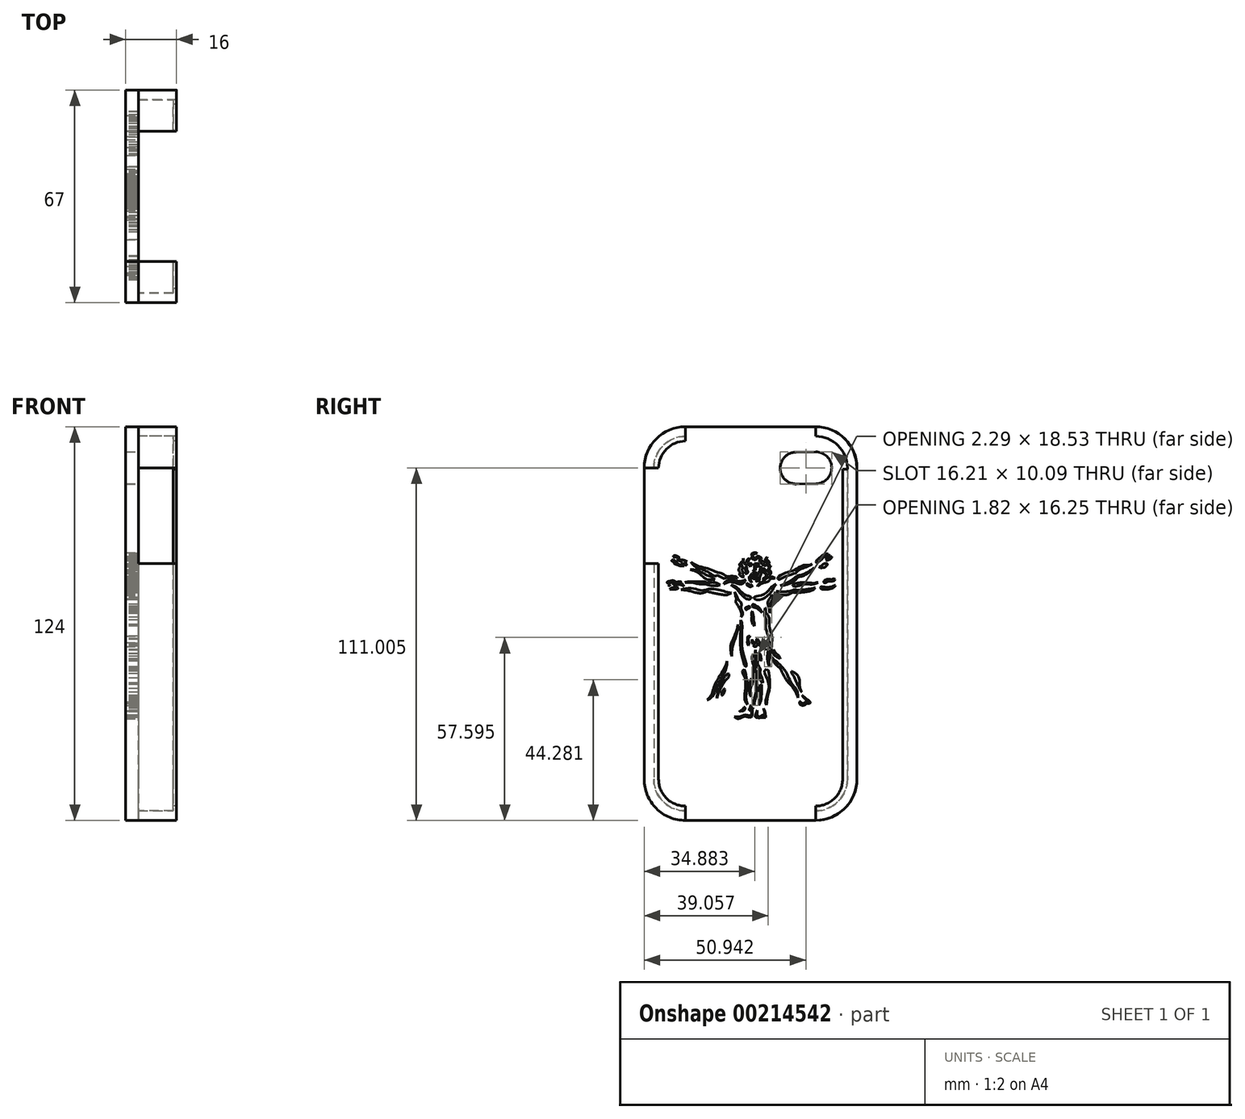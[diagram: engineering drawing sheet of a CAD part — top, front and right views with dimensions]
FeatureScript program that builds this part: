
annotation { "Feature Type Name" : "Feature", "Feature Type Description" : "" }
export const myFeature = defineFeature(function(context is Context, id is Id, definition is map)
    precondition{}
    {
        {
            var Q0;
            Q0=qCreatedBy(makeId("Right.planeOp"),FACE);
            var sketch = newSketch(context, id + "F0", { "sketchPlane" : qUnion([Q0])});
            skLineSegment(sketch, "E0.rect.bottom", {"start": v(20.5, 62) * mm, "end": v(-20.5, 62) * mm});
            skLineSegment(sketch, "E0.rect.top", {"start": v(20.5, -62) * mm, "end": v(-20.5, -62) * mm});
            skLineSegment(sketch, "E0.rect.left", {"start": v(33.5, 49) * mm, "end": v(33.5, -49) * mm});
            skLineSegment(sketch, "E0.rect.right", {"start": v(-33.5, 49) * mm, "end": v(-33.5, -49) * mm});
            skPoint(sketch, "E0.rect.middle", {"position": v(0, 0) * mm});
            skPoint(sketch, "E1.visualSharp", {"position": v(-33.5, 62) * mm});
            skArc(sketch, "E1.filletArc", {"start": v(-20.5, 62) * mm, "mid": v(-29.7, 58.2) * mm, "end": v(-33.5, 49) * mm});
            skPoint(sketch, "E2.visualSharp", {"position": v(-33.5, -62) * mm});
            skArc(sketch, "E2.filletArc", {"start": v(-33.5, -49) * mm, "mid": v(-29.7, -58.2) * mm, "end": v(-20.5, -62) * mm});
            skPoint(sketch, "E3.visualSharp", {"position": v(33.5, 62) * mm});
            skArc(sketch, "E3.filletArc", {"start": v(33.5, 49) * mm, "mid": v(29.7, 58.2) * mm, "end": v(20.5, 62) * mm});
            skPoint(sketch, "E4.visualSharp", {"position": v(33.5, -62) * mm});
            skArc(sketch, "E4.filletArc", {"start": v(20.5, -62) * mm, "mid": v(29.7, -58.2) * mm, "end": v(33.5, -49) * mm});
            skSolve(sketch);
        }
        {
            var Q0;
            Q0=qSketchRegion(id+"F0",true);
            extrude(context, id + "F1", {"entities" : qUnion([Q0]), "depth" : 4 * mm});
        }
        {
            var Q0;
            Q0=qCreatedBy(makeId("Right.planeOp"),FACE);
            var sketch = newSketch(context, id + "F2", { "sketchPlane" : qUnion([Q0])});
            skArc(sketch, "E5", {"start": v(20.7, 44.05) * mm, "mid": v(25.55, 49.12) * mm, "end": v(20.55, 54.05) * mm});
            skLineSegment(sketch, "E6", {"start": v(20.55, 54.05) * mm, "end": v(14.26, 53.96) * mm});
            skLineSegment(sketch, "E7", {"start": v(20.7, 44.05) * mm, "end": v(14.4, 43.96) * mm});
            skArc(sketch, "E8", {"start": v(14.26, 53.96) * mm, "mid": v(9.34, 48.89) * mm, "end": v(14.4, 43.96) * mm});
            skLineSegment(sketch, "E9", {"start": v(14.26, 53.96) * mm, "end": v(14.4, 43.96) * mm, "construction": true});
            skLineSegment(sketch, "E10", {"start": v(20.55, 54.05) * mm, "end": v(20.7, 44.05) * mm, "construction": true});
            skSolve(sketch);
        }
        {
            var Q0;
            Q0=makeQuery(id+"F2.imprint","IMPRINT",FACE,{"disambiguationData":[TD([[makeQuery(id+"F2.imprint","IMPRINT",EDGE,{"derivedFrom":sQuery(id+"F2.wireOp",EDGE,"E5")}),1.0]])]});
            extrude(context, id + "F3", {"entities" : qUnion([Q0]), "operationType" : NewBodyOperationType.REMOVE, "oppositeDirection" : true, "depth" : 25.4 * mm, "hasSecondDirection" : true, "secondDirectionOppositeDirection" : false, "secondDirectionDepth" : 33.72 * mm});
        }
        {
            var Q0;
            Q0=qCreatedBy(makeId("Right.planeOp"),FACE);
            var sketch = newSketch(context, id + "F4", { "sketchPlane" : qUnion([Q0])});
            skLineSegment(sketch, "E11", {"start": v(-30.46, 18.92) * mm, "end": v(-33.5, 18.92) * mm});
            skLineSegment(sketch, "E12", {"start": v(-33.5, 18.92) * mm, "end": v(-33.5, -49) * mm});
            skLineSegment(sketch, "E13", {"start": v(-33.5, -49) * mm, "end": v(-30.46, -49) * mm});
            skLineSegment(sketch, "E14", {"start": v(-30.46, -49) * mm, "end": v(-30.46, 18.92) * mm});
            skSolve(sketch);
        }
        {
            var Q0;
            Q0=qSketchRegion(id+"F4",true);
            extrude(context, id + "F5", {"entities" : qUnion([Q0]), "operationType" : NewBodyOperationType.ADD, "depth" : 16 * mm});
        }
        {
            var Q0;
            Q0=qCreatedBy(makeId("Right.planeOp"),FACE);
            var sketch = newSketch(context, id + "F6", { "sketchPlane" : qUnion([Q0])});
            skLineSegment(sketch, "E15", {"start": v(-33.5, -49) * mm, "end": v(-30.46, -49) * mm});
            skLineSegment(sketch, "E16", {"start": v(-20.5, -59) * mm, "end": v(-20.5, -62) * mm});
            skArc(sketch, "E17", {"start": v(-30.46, -49) * mm, "mid": v(-27.56, -56.07) * mm, "end": v(-20.5, -59) * mm});
            skArc(sketch, "E18", {"start": v(-33.5, -49) * mm, "mid": v(-29.7, -58.2) * mm, "end": v(-20.5, -62) * mm});
            skSolve(sketch);
        }
        {
            var Q0;
            Q0=qSketchRegion(id+"F6",true);
            extrude(context, id + "F7", {"entities" : qUnion([Q0]), "operationType" : NewBodyOperationType.ADD, "depth" : 16 * mm});
        }
        {
            var Q0;
            Q0=qCreatedBy(makeId("Right.planeOp"),FACE);
            var sketch = newSketch(context, id + "F8", { "sketchPlane" : qUnion([Q0])});
            skLineSegment(sketch, "E19", {"start": v(-30.47, 48.93) * mm, "end": v(-33.5, 48.93) * mm});
            skLineSegment(sketch, "E20", {"start": v(-20.5, 62) * mm, "end": v(-20.5, 58.97) * mm});
            skArc(sketch, "E21", {"start": v(-20.5, 58.97) * mm, "mid": v(-27.55, 56) * mm, "end": v(-30.47, 48.93) * mm});
            skArc(sketch, "E22", {"start": v(-20.5, 62) * mm, "mid": v(-29.7, 58.15) * mm, "end": v(-33.5, 48.93) * mm});
            skSolve(sketch);
        }
        {
            var Q0;
            Q0=qSketchRegion(id+"F8",true);
            extrude(context, id + "F9", {"entities" : qUnion([Q0]), "operationType" : NewBodyOperationType.ADD, "depth" : 16 * mm});
        }
        {
            var Q0;
            Q0=qCreatedBy(makeId("Right.planeOp"),FACE);
            var sketch = newSketch(context, id + "F10", { "sketchPlane" : qUnion([Q0])});
            skLineSegment(sketch, "E23", {"start": v(20.49, -62) * mm, "end": v(20.49, -59) * mm});
            skLineSegment(sketch, "E24", {"start": v(33.5, -49) * mm, "end": v(30.5, -49) * mm});
            skArc(sketch, "E25", {"start": v(20.49, -59) * mm, "mid": v(27.55, -56.06) * mm, "end": v(30.5, -49) * mm});
            skArc(sketch, "E26", {"start": v(20.49, -62) * mm, "mid": v(29.67, -58.19) * mm, "end": v(33.5, -49) * mm});
            skSolve(sketch);
        }
        {
            var Q0;
            Q0=qSketchRegion(id+"F10",true);
            extrude(context, id + "F11", {"entities" : qUnion([Q0]), "operationType" : NewBodyOperationType.ADD, "depth" : 16 * mm});
        }
        {
            var Q0;
            Q0=qCreatedBy(makeId("Right.planeOp"),FACE);
            var sketch = newSketch(context, id + "F12", { "sketchPlane" : qUnion([Q0])});
            skLineSegment(sketch, "E27", {"start": v(33.46, 49) * mm, "end": v(30.5, 49) * mm});
            skLineSegment(sketch, "E28", {"start": v(20.5, 62) * mm, "end": v(20.5, 58.99) * mm});
            skArc(sketch, "E29", {"start": v(33.46, 49) * mm, "mid": v(29.66, 58.17) * mm, "end": v(20.5, 62) * mm});
            skArc(sketch, "E30", {"start": v(30.5, 49) * mm, "mid": v(27.55, 56.05) * mm, "end": v(20.5, 58.99) * mm});
            skSolve(sketch);
        }
        {
            var Q0;
            Q0=qSketchRegion(id+"F12",true);
            extrude(context, id + "F13", {"entities" : qUnion([Q0]), "operationType" : NewBodyOperationType.ADD, "depth" : 16 * mm});
        }
        {
            var Q0;
            Q0=qCreatedBy(makeId("Right.planeOp"),FACE);
            var sketch = newSketch(context, id + "F14", { "sketchPlane" : qUnion([Q0])});
            skLineSegment(sketch, "E31", {"start": v(30.5, -49) * mm, "end": v(33.49, -49) * mm});
            skLineSegment(sketch, "E32", {"start": v(33.49, -49) * mm, "end": v(33.49, 49) * mm});
            skLineSegment(sketch, "E33", {"start": v(33.49, 49) * mm, "end": v(30.5, 49) * mm});
            skLineSegment(sketch, "E34", {"start": v(30.5, 49) * mm, "end": v(30.5, -49) * mm});
            skSolve(sketch);
        }
        {
            var Q0;
            Q0=qSketchRegion(id+"F14",true);
            extrude(context, id + "F15", {"entities" : qUnion([Q0]), "operationType" : NewBodyOperationType.ADD, "depth" : 16 * mm});
        }
        {
            var Q0;
            Q0=qCreatedBy(makeId("Right.planeOp"),FACE);
            var sketch = newSketch(context, id + "F16", { "sketchPlane" : qUnion([Q0])});
            skLineSegment(sketch, "E35", {"start": v(-30.46, 18.92) * mm, "end": v(-30.46, -49.07) * mm});
            skLineSegment(sketch, "E36", {"start": v(-30.46, -49.07) * mm, "end": v(-28.96, -49.07) * mm});
            skLineSegment(sketch, "E37", {"start": v(-28.96, -49.07) * mm, "end": v(-28.96, 18.92) * mm});
            skLineSegment(sketch, "E38", {"start": v(-28.96, 18.92) * mm, "end": v(-30.46, 18.92) * mm});
            skLineSegment(sketch, "E39", {"start": v(-20.5, -59) * mm, "end": v(-20.5, -57.5) * mm});
            skArc(sketch, "E40", {"start": v(-30.46, -49.07) * mm, "mid": v(-27.53, -56.1) * mm, "end": v(-20.5, -59) * mm});
            skArc(sketch, "E41", {"start": v(-28.96, -49.07) * mm, "mid": v(-26.47, -55.04) * mm, "end": v(-20.5, -57.5) * mm});
            skLineSegment(sketch, "E42", {"start": v(-30.47, 48.93) * mm, "end": v(-28.97, 48.93) * mm});
            skLineSegment(sketch, "E43", {"start": v(-20.5, 58.97) * mm, "end": v(-20.5, 57.47) * mm});
            skArc(sketch, "E44", {"start": v(-20.5, 58.97) * mm, "mid": v(-27.55, 56) * mm, "end": v(-30.47, 48.93) * mm});
            skArc(sketch, "E45", {"start": v(-20.5, 57.47) * mm, "mid": v(-26.5, 54.95) * mm, "end": v(-28.97, 48.93) * mm});
            skLineSegment(sketch, "E46", {"start": v(30.5, 48.62) * mm, "end": v(29, 48.62) * mm});
            skLineSegment(sketch, "E47", {"start": v(30.5, -49) * mm, "end": v(29, -49) * mm});
            skLineSegment(sketch, "E48", {"start": v(29, -49) * mm, "end": v(29, 48.62) * mm});
            skLineSegment(sketch, "E49", {"start": v(30.5, 48.62) * mm, "end": v(30.5, -49) * mm});
            skLineSegment(sketch, "E50", {"start": v(20.49, -59) * mm, "end": v(20.49, -57.5) * mm});
            skArc(sketch, "E51", {"start": v(20.49, -59) * mm, "mid": v(27.54, -56.06) * mm, "end": v(30.5, -49) * mm});
            skArc(sketch, "E52", {"start": v(20.49, -57.5) * mm, "mid": v(26.5, -55.02) * mm, "end": v(29, -49) * mm});
            skSolve(sketch);
        }
        {
            var Q0;
            Q0=qSketchRegion(id+"F16",true);
            extrude(context, id + "F17", {"entities" : qUnion([Q0]), "operationType" : NewBodyOperationType.ADD, "depth" : 16 * mm, "hasSecondDirection" : true, "secondDirectionOppositeDirection" : false, "secondDirectionDepth" : 15 * mm});
        }
        {
            var Q0;
            Q0=makeQuery(id+"F7.boolean.opBoolean","MERGE",FACE,{"derivedFrom":[makeQuery(id+"F1.opExtrude","CAP_FACE",FACE,{"disambiguationData":[OSD([sQuery(id+"F0.wireOp",EDGE,"E0.rect.bottom"),sQuery(id+"F0.wireOp",EDGE,"E0.rect.top"),sQuery(id+"F0.wireOp",EDGE,"E0.rect.left"),sQuery(id+"F0.wireOp",EDGE,"E0.rect.right"),sQuery(id+"F0.wireOp",EDGE,"E1.filletArc"),sQuery(id+"F0.wireOp",EDGE,"E2.filletArc"),sQuery(id+"F0.wireOp",EDGE,"E3.filletArc"),sQuery(id+"F0.wireOp",EDGE,"E4.filletArc")])],"isStart":true}),makeQuery(id+"F7.opExtrude","CAP_FACE",FACE,{"disambiguationData":[OSD([sQuery(id+"F6.wireOp",EDGE,"E15"),sQuery(id+"F6.wireOp",EDGE,"E16"),sQuery(id+"F6.wireOp",EDGE,"E17"),sQuery(id+"F6.wireOp",EDGE,"E18")])],"isStart":true})]});
            var sketch = newSketch(context, id + "F18", { "sketchPlane" : qUnion([Q0])});
            skFitSpline(sketch, "E53", {"points": [v(-5.3, 20.95) * mm, v(-5.08, 20.49) * mm, v(-5.07, 20.23) * mm, v(-5.38, 19.94) * mm, v(-5.8, 19.52) * mm, v(-5.97, 19.03) * mm, v(-5.91, 18.5) * mm, v(-5.56, 18.14) * mm, v(-5.18, 18.05) * mm], "startDerivative": vector(1.98, -3.71) * mm, "endDerivative": vector(3.27, -0.38) * mm});
            skFitSpline(sketch, "E54", {"points": [v(-5.18, 18.05) * mm, v(-5.38, 18.43) * mm, v(-5.42, 18.75) * mm, v(-5, 19.2) * mm, v(-4.59, 19.79) * mm, v(-4.8, 20.49) * mm, v(-5.3, 20.95) * mm], "startDerivative": vector(-1.44, 2.71) * mm, "endDerivative": vector(-3, 2.18) * mm});
            skFitSpline(sketch, "E55", {"points": [v(-4.86, 18.31) * mm, v(-4.38, 18.48) * mm, v(-4.08, 18.63) * mm, v(-4.13, 18.82) * mm, v(-4.34, 18.92) * mm, v(-4.43, 19.12) * mm, v(-4.16, 19.45) * mm, v(-3.79, 19.73) * mm, v(-3.31, 19.92) * mm, v(-2.83, 19.95) * mm, v(-2.48, 19.94) * mm], "startDerivative": vector(4.03, 1.47) * mm, "endDerivative": vector(3.46, -0.17) * mm});
            skFitSpline(sketch, "E56", {"points": [v(-2.48, 19.94) * mm, v(-2.97, 19.62) * mm, v(-3.4, 19.33) * mm, v(-3.43, 19.04) * mm, v(-3.65, 18.67) * mm, v(-3.97, 18.39) * mm, v(-4.86, 18.31) * mm], "startDerivative": vector(-2.59, -1.79) * mm, "endDerivative": vector(-4.64, 0.1) * mm});
            skFitSpline(sketch, "E57", {"points": [v(-3.52, 20.35) * mm, v(-3.28, 20.77) * mm, v(-2.76, 21.13) * mm, v(-2.08, 21.13) * mm, v(-1.65, 20.74) * mm, v(-1.47, 20.55) * mm, v(-1.05, 20.77) * mm, v(-0.8, 21.13) * mm, v(-0.75, 21.42) * mm], "startDerivative": vector(1.54, 3.4) * mm, "endDerivative": vector(0.15, 2.97) * mm});
            skFitSpline(sketch, "E58", {"points": [v(-3.52, 20.35) * mm, v(-3.12, 20.55) * mm, v(-2.72, 20.7) * mm, v(-2.14, 20.55) * mm, v(-1.62, 20.08) * mm, v(-1.12, 20.05) * mm, v(-0.59, 20.35) * mm, v(-0.3, 20.72) * mm, v(-0.53, 21.23) * mm, v(-0.75, 21.42) * mm], "startDerivative": vector(3.9, 1.83) * mm, "endDerivative": vector(-2.52, 1.75) * mm});
            skFitSpline(sketch, "E59", {"points": [v(-2.15, 22.03) * mm, v(-1.67, 22.32) * mm, v(-0.96, 22.29) * mm, v(-0.38, 21.97) * mm, v(-0.3, 21.4) * mm], "startDerivative": vector(1.86, 1.47) * mm, "endDerivative": vector(-0.08, -2.6) * mm});
            skFitSpline(sketch, "E60", {"points": [v(-0.3, 21.4) * mm, v(-0.62, 21.7) * mm, v(-1.08, 21.9) * mm, v(-1.53, 22) * mm, v(-2.15, 22.03) * mm], "startDerivative": vector(-1.27, 1.38) * mm, "endDerivative": vector(-2.36, 0.03) * mm});
            skFitSpline(sketch, "E61", {"points": [v(0.14, 20.17) * mm, v(0.42, 20.08) * mm, v(0.63, 19.76) * mm, v(0.63, 19.2) * mm, v(0.78, 18.78) * mm, v(1.23, 18.52) * mm, v(1.5, 18.55) * mm, v(1.85, 18.76) * mm, v(2.06, 19.18) * mm], "startDerivative": vector(2.8, -0.46) * mm, "endDerivative": vector(1.18, 3.47) * mm});
            skLineSegment(sketch, "E62", {"start": v(2.06, 19.18) * mm, "end": v(1.36, 19.18) * mm});
            skFitSpline(sketch, "E63", {"points": [v(0.14, 20.17) * mm, v(0.42, 20.35) * mm, v(0.85, 20.32) * mm, v(1.21, 19.82) * mm, v(1.36, 19.18) * mm], "startDerivative": vector(1.24, 1.03) * mm, "endDerivative": vector(0.37, -2.24) * mm});
            skFitSpline(sketch, "E64", {"points": [v(-5.2, 16.73) * mm, v(-4.9, 16.77) * mm, v(-4.6, 16.92) * mm, v(-4.42, 17.1) * mm, v(-4.29, 17.45) * mm], "startDerivative": vector(1.26, 0.08) * mm, "endDerivative": vector(0.46, 1.4) * mm});
            skFitSpline(sketch, "E65", {"points": [v(-4.29, 17.45) * mm, v(-4.05, 17.21) * mm, v(-3.88, 16.94) * mm, v(-3.85, 16.49) * mm, v(-4.1, 16.1) * mm, v(-4.48, 15.84) * mm, v(-4.85, 15.41) * mm, v(-4.82, 14.96) * mm, v(-4.67, 14.72) * mm], "startDerivative": vector(2.24, -2.1) * mm, "endDerivative": vector(1.59, -2.04) * mm});
            skFitSpline(sketch, "E66", {"points": [v(-4.67, 14.72) * mm, v(-5.06, 14.79) * mm, v(-5.2, 15.34) * mm, v(-5.1, 15.72) * mm, v(-4.72, 16.06) * mm, v(-4.55, 16.38) * mm, v(-4.55, 16.67) * mm], "startDerivative": vector(-2.73, -0.18) * mm, "endDerivative": vector(-0.2, 2.07) * mm});
            skLineSegment(sketch, "E67", {"start": v(-5.2, 16.73) * mm, "end": v(-4.55, 16.67) * mm});
            skFitSpline(sketch, "E68", {"points": [v(-6.41, 18.26) * mm, v(-5.88, 17.73) * mm, v(-5.62, 17.28) * mm, v(-5.51, 16.74) * mm, v(-5.72, 16.23) * mm, v(-5.94, 15.92) * mm, v(-5.86, 15.76) * mm, v(-5.72, 15.55) * mm, v(-5.94, 15.4) * mm, v(-6.35, 15.64) * mm, v(-6.41, 16.1) * mm, v(-6.19, 16.65) * mm, v(-5.96, 17.08) * mm, v(-6.06, 17.55) * mm, v(-6.41, 18.26) * mm]});
            skFitSpline(sketch, "E69", {"points": [v(2.32, 20.56) * mm, v(2.34, 19.96) * mm, v(2.72, 19.5) * mm, v(3.13, 19.07) * mm, v(3.42, 18.78) * mm], "startDerivative": vector(-0.25, -2.42) * mm, "endDerivative": vector(1.32, -1.28) * mm});
            skFitSpline(sketch, "E70", {"points": [v(3.42, 18.78) * mm, v(3.55, 18.6) * mm, v(3.33, 18.16) * mm, v(3.33, 17.7) * mm, v(3.6, 17.4) * mm, v(3.74, 16.95) * mm, v(3.62, 16.54) * mm, v(3.42, 16.29) * mm, v(3.33, 16.11) * mm, v(3.42, 15.8) * mm, v(3.42, 15.36) * mm, v(3.18, 15.08) * mm, v(2.85, 14.82) * mm, v(2.29, 14.67) * mm], "startDerivative": vector(3.4, -2.6) * mm, "endDerivative": vector(-6.53, -1.1) * mm});
            skFitSpline(sketch, "E71", {"points": [v(2.29, 14.67) * mm, v(1.92, 14.67) * mm], "startDerivative": vector(-0.36, 0) * mm, "endDerivative": vector(-0.36, 0) * mm});
            skFitSpline(sketch, "E72", {"points": [v(1.92, 14.69) * mm, v(2.29, 14.97) * mm, v(2.52, 15.32) * mm, v(2.53, 15.54) * mm, v(2.4, 15.8) * mm, v(2.29, 16) * mm, v(2.5, 16.34) * mm, v(2.65, 16.67) * mm, v(2.79, 16.99) * mm, v(2.56, 17.24) * mm, v(2.44, 17.67) * mm, v(2.6, 18.12) * mm, v(2.83, 18.64) * mm, v(2.68, 19.13) * mm, v(2.29, 19.64) * mm, v(2.32, 20.56) * mm], "startDerivative": vector(5.52, 3.67) * mm, "endDerivative": vector(1.89, 10.32) * mm});
            skFitSpline(sketch, "E73", {"points": [v(0.92, 17.78) * mm, v(1.31, 17.82) * mm, v(1.6, 17.74) * mm, v(1.72, 17.37) * mm, v(1.64, 16.96) * mm, v(1.48, 16.47) * mm, v(1.48, 16.02) * mm, v(1.75, 15.7) * mm], "startDerivative": vector(2.86, 0.43) * mm, "endDerivative": vector(2.32, -1.97) * mm});
            skFitSpline(sketch, "E74", {"points": [v(1.75, 15.7) * mm, v(1.3, 15.7) * mm, v(0.93, 15.94) * mm, v(0.85, 16.42) * mm, v(1.05, 16.77) * mm, v(1.2, 17.08) * mm, v(1.24, 17.34) * mm, v(0.92, 17.78) * mm], "startDerivative": vector(-3.06, -0.3) * mm, "endDerivative": vector(-2.68, 2.8) * mm});
            skFitSpline(sketch, "E75", {"points": [v(-1.88, 15.87) * mm, v(-1.71, 16.09) * mm, v(-1.32, 16.24) * mm, v(-0.94, 16.13) * mm, v(-0.6, 15.98) * mm], "startDerivative": vector(0.58, 1.05) * mm, "endDerivative": vector(1.29, -0.6) * mm});
            skFitSpline(sketch, "E76", {"points": [v(-1.88, 15.87) * mm, v(-1.5, 15.95) * mm, v(-1.23, 15.97) * mm, v(-0.6, 15.98) * mm], "startDerivative": vector(1.27, 0.29) * mm, "endDerivative": vector(1.7, 0.04) * mm});
            skFitSpline(sketch, "E77", {"points": [v(-3.4, 18.19) * mm, v(-3.16, 17.57) * mm, v(-2.99, 16.91) * mm, v(-2.99, 16.55) * mm], "startDerivative": vector(0.73, -1.63) * mm, "endDerivative": vector(-0.1, -1.24) * mm});
            skFitSpline(sketch, "E78", {"points": [v(-2.99, 16.55) * mm, v(-2.66, 16.23) * mm, v(-2.44, 15.82) * mm, v(-2.24, 15.2) * mm, v(-1.95, 14.87) * mm, v(-1.34, 14.85) * mm, v(-0.8, 14.84) * mm, v(-0.45, 15.14) * mm, v(0, 15.63) * mm], "startDerivative": vector(2.94, -2.73) * mm, "endDerivative": vector(3.37, 3.51) * mm});
            skFitSpline(sketch, "E79", {"points": [v(0, 15.63) * mm, v(-0.27, 14.95) * mm, v(-0.56, 14.45) * mm, v(-0.87, 14.1) * mm, v(-1.66, 14.17) * mm, v(-1.92, 14.22) * mm], "startDerivative": vector(-1.1, -3.09) * mm, "endDerivative": vector(-1.49, 0.22) * mm});
            skFitSpline(sketch, "E80", {"points": [v(-1.92, 14.22) * mm, v(-1.85, 13.66) * mm, v(-1.85, 13.22) * mm, v(-2.2, 13.77) * mm, v(-2.4, 14.21) * mm, v(-2.52, 14.5) * mm], "startDerivative": vector(0.3, -2.37) * mm, "endDerivative": vector(-0.82, 1.75) * mm});
            skFitSpline(sketch, "E81", {"points": [v(-2.52, 14.5) * mm, v(-2.68, 14.4) * mm, v(-2.65, 14.21) * mm], "startDerivative": vector(-0.42, -0.14) * mm, "endDerivative": vector(0.16, -0.43) * mm});
            skFitSpline(sketch, "E82", {"points": [v(-2.65, 14.21) * mm, v(-2.65, 13.87) * mm, v(-2.65, 13.32) * mm, v(-2.65, 13.06) * mm], "startDerivative": vector(0, -0.98) * mm, "endDerivative": vector(0, -0.82) * mm});
            skFitSpline(sketch, "E83", {"points": [v(-2.65, 13.06) * mm, v(-2.81, 13.72) * mm, v(-2.9, 14.4) * mm, v(-3.16, 15.21) * mm, v(-3.4, 16.03) * mm, v(-3.4, 16.94) * mm, v(-3.4, 18.19) * mm], "startDerivative": vector(-1.3, 4.46) * mm, "endDerivative": vector(-0.08, 6.47) * mm});
            skFitSpline(sketch, "E84", {"points": [v(-0.27, 12.9) * mm, v(0, 13.75) * mm, v(0.17, 14.4) * mm, v(0.24, 14.8) * mm, v(0.43, 14.73) * mm, v(0.41, 14.21) * mm, v(0.32, 13.75) * mm, v(0.12, 13.32) * mm, v(-0.27, 12.9) * mm]});
            skFitSpline(sketch, "E85", {"points": [v(-0.67, 11.9) * mm, v(-0.22, 12.04) * mm, v(0.37, 12.28) * mm, v(0.82, 12.52) * mm, v(1.22, 12.82) * mm], "startDerivative": vector(1.83, 0.5) * mm, "endDerivative": vector(1.64, 1.3) * mm});
            skFitSpline(sketch, "E86", {"points": [v(1.22, 12.82) * mm, v(1.22, 12.23) * mm, v(0.8, 11.87) * mm, v(0.52, 11.66) * mm, v(0, 11.57) * mm, v(-0.67, 11.9) * mm], "startDerivative": vector(0.61, -3.08) * mm, "endDerivative": vector(-2.85, 1.9) * mm});
            skFitSpline(sketch, "E87", {"points": [v(1.48, 13.8) * mm, v(2.16, 12.82) * mm, v(3.08, 12.35) * mm, v(3.78, 12.52) * mm, v(4.92, 12.82) * mm, v(6.46, 13.13) * mm, v(7.55, 12.82) * mm, v(8.45, 12.38) * mm], "startDerivative": vector(3.85, -7.17) * mm, "endDerivative": vector(6.46, -3.26) * mm});
            skFitSpline(sketch, "E88", {"points": [v(8.45, 12.38) * mm, v(7.94, 13.19) * mm, v(6.82, 13.6) * mm, v(5.96, 13.66) * mm, v(5.2, 13.55) * mm, v(4.22, 13.33) * mm, v(3.13, 13.33) * mm, v(2.3, 13.44) * mm, v(1.48, 13.8) * mm], "startDerivative": vector(-2.96, 7.18) * mm, "endDerivative": vector(-6.66, 3.53) * mm});
            skFitSpline(sketch, "E89", {"points": [v(4.13, 14.21) * mm, v(4.29, 14.62) * mm, v(4.89, 14.88) * mm, v(5.84, 14.9) * mm, v(6.67, 14.88) * mm, v(7.66, 14.88) * mm, v(8.23, 15.35) * mm, v(9.28, 15.83) * mm, v(10, 15.96) * mm, v(11.06, 16.3) * mm, v(11.85, 16.75) * mm, v(12.65, 17.04) * mm, v(13.8, 17.39) * mm, v(14.65, 17.58) * mm, v(15.76, 17.9) * mm, v(16.97, 18.31) * mm, v(18.72, 19.36) * mm], "startDerivative": vector(2.07, 10.7) * mm, "endDerivative": vector(20.02, 13.25) * mm});
            skFitSpline(sketch, "E90", {"points": [v(18.72, 19.36) * mm, v(17.83, 18.18) * mm, v(17.2, 17.74) * mm, v(16.2, 17.39) * mm, v(15.13, 16.98) * mm, v(13.8, 16.44) * mm, v(12.77, 15.86) * mm, v(11.53, 15.07) * mm, v(10.9, 15) * mm, v(10.42, 15.26) * mm], "startDerivative": vector(-6.96, -10.12) * mm, "endDerivative": vector(-5.77, 3.88) * mm});
            skFitSpline(sketch, "E91", {"points": [v(10.42, 15.26) * mm, v(8.39, 14.18) * mm], "startDerivative": vector(-2.03, -1.08) * mm, "endDerivative": vector(-2.03, -1.08) * mm});
            skFitSpline(sketch, "E92", {"points": [v(8.39, 14.18) * mm, v(7.14, 14.45) * mm, v(5.83, 14.4) * mm, v(4.13, 14.21) * mm], "startDerivative": vector(-3.95, 1.13) * mm, "endDerivative": vector(-4.82, -0.51) * mm});
            skFitSpline(sketch, "E93", {"points": [v(6.12, 12.13) * mm, v(5.14, 11.87) * mm, v(4.45, 11.44) * mm, v(3.54, 10.64) * mm, v(2.71, 9.82) * mm, v(1.87, 9.15) * mm, v(1.1, 8.8) * mm, v(0.46, 8.68) * mm, v(0, 8.41) * mm, v(-0.25, 7.81) * mm], "startDerivative": vector(-8.69, -1.88) * mm, "endDerivative": vector(-1.93, -6.98) * mm});
            skFitSpline(sketch, "E94", {"points": [v(-0.25, 7.81) * mm, v(0, 7.79) * mm, v(0.42, 7.63) * mm, v(0.82, 7.66) * mm, v(1.33, 7.79) * mm, v(2.29, 8.41) * mm, v(2.8, 9.01) * mm, v(3.45, 9.75) * mm, v(4.16, 10.62) * mm, v(5.16, 11.38) * mm, v(6.12, 12.13) * mm], "startDerivative": vector(4.1, 0.13) * mm, "endDerivative": vector(7.37, 6.13) * mm});
            skFitSpline(sketch, "E95", {"points": [v(-8.02, 12.37) * mm, v(-7.45, 11.61) * mm, v(-6.96, 10.68) * mm, v(-6.52, 9.95) * mm, v(-5.48, 8.9) * mm, v(-4.03, 7.83) * mm, v(-2.6, 7.5) * mm, v(-1.46, 7.67) * mm, v(-1.05, 8.11) * mm, v(-1.33, 8.45) * mm, v(-1.88, 8.63) * mm, v(-2.68, 8.71) * mm, v(-3.93, 9.02) * mm, v(-5.3, 10.06) * mm, v(-6.1, 10.94) * mm, v(-6.88, 11.74) * mm, v(-8.02, 12.37) * mm]});
            skFitSpline(sketch, "E96", {"points": [v(-2.18, 11.71) * mm, v(-3.08, 12.32) * mm, v(-4.24, 12.83) * mm, v(-5.63, 13.27) * mm, v(-6.02, 13.7) * mm, v(-6.4, 14.1) * mm, v(-7.28, 14.14) * mm, v(-7.65, 14.36) * mm], "startDerivative": vector(-5.44, 3.93) * mm, "endDerivative": vector(-2.91, 2.78) * mm});
            skFitSpline(sketch, "E97", {"points": [v(-7.65, 14.36) * mm, v(-7.06, 14.65) * mm, v(-6.63, 14.75) * mm, v(-5.8, 14.56) * mm, v(-5.2, 14.29) * mm, v(-4.82, 14.05) * mm], "startDerivative": vector(2.95, 1.56) * mm, "endDerivative": vector(2.05, -1.44) * mm});
            skFitSpline(sketch, "E98", {"points": [v(-4.82, 14.05) * mm, v(-4.3, 14.27) * mm, v(-3.91, 14.05) * mm, v(-4.18, 13.73) * mm, v(-4.43, 13.44) * mm, v(-4.12, 13.27) * mm, v(-3.4, 12.92) * mm, v(-2.84, 12.54) * mm, v(-2.43, 12.23) * mm, v(-2.18, 11.71) * mm], "startDerivative": vector(4.21, 2.98) * mm, "endDerivative": vector(1.83, -4.88) * mm});
            skFitSpline(sketch, "E99", {"points": [v(-19.43, 18.71) * mm, v(-18.4, 18.37) * mm, v(-17.85, 18.4) * mm, v(-16.92, 18.4) * mm, v(-16.06, 18.08) * mm, v(-14.93, 17.62) * mm, v(-14.16, 16.92) * mm, v(-13.32, 16.55) * mm, v(-12.42, 16.4) * mm, v(-11.36, 16.1) * mm, v(-10.06, 15.48) * mm, v(-9.14, 15) * mm, v(-8.56, 14.3) * mm, v(-8.85, 13.8) * mm, v(-10.67, 14.65) * mm, v(-12, 15.14) * mm, v(-13.35, 15.63) * mm, v(-14.16, 15.8) * mm], "startDerivative": vector(18.97, -7.69) * mm, "endDerivative": vector(-14.39, 2.28) * mm});
            skFitSpline(sketch, "E100", {"points": [v(-14.16, 15.8) * mm, v(-14.73, 16.46) * mm, v(-16.06, 17.24) * mm, v(-17.41, 17.79) * mm, v(-19.43, 18.71) * mm], "startDerivative": vector(-2.48, 3.48) * mm, "endDerivative": vector(-6.97, 3.32) * mm});
            skArc(sketch, "E101", {"start": v(-19.98, 17.62) * mm, "mid": v(-17.48, 15.91) * mm, "end": v(-14.59, 15.02) * mm});
            skArc(sketch, "E102", {"start": v(-19.98, 17.62) * mm, "mid": v(-17.77, 15.63) * mm, "end": v(-14.98, 14.6) * mm});
            skArc(sketch, "E103", {"start": v(-14.98, 14.6) * mm, "mid": v(-12.48, 12.64) * mm, "end": v(-9.38, 11.95) * mm});
            skFitSpline(sketch, "E104", {"points": [v(-14.59, 15.02) * mm, v(-13.75, 14.28) * mm, v(-11.87, 13) * mm, v(-10.34, 12.3) * mm, v(-9.38, 11.95) * mm], "startDerivative": vector(3.38, -3.16) * mm, "endDerivative": vector(4.45, -1.53) * mm});
            skFitSpline(sketch, "E105", {"points": [v(-21.51, 17.9) * mm, v(-21.93, 17.97) * mm, v(-22.48, 18.38) * mm, v(-23.13, 18.8) * mm, v(-23.82, 18.91) * mm, v(-24.15, 18.8) * mm, v(-24.11, 18.48) * mm, v(-23.73, 18.02) * mm, v(-23.3, 17.71) * mm, v(-22.75, 17.58) * mm, v(-22.17, 17.51) * mm, v(-21.79, 17.68) * mm, v(-21.51, 17.9) * mm]});
            skFitSpline(sketch, "E106", {"points": [v(-24.5, 21.93) * mm, v(-23.86, 21.75) * mm, v(-23.39, 21.31) * mm, v(-22.95, 20.8) * mm, v(-22.22, 20.06) * mm, v(-21.66, 19.55) * mm, v(-20.97, 19.15) * mm, v(-20.66, 19.24) * mm, v(-20.71, 19.62) * mm, v(-21.13, 20.17) * mm, v(-22.3, 21.22) * mm, v(-23.37, 21.84) * mm, v(-24.5, 21.93) * mm]});
            skArc(sketch, "E107", {"start": v(-23.75, 19.91) * mm, "mid": v(-24.59, 20.73) * mm, "end": v(-25.7, 21.13) * mm});
            skArc(sketch, "E108", {"start": v(-25.7, 21.13) * mm, "mid": v(-24.92, 20.2) * mm, "end": v(-23.75, 19.91) * mm});
            skArc(sketch, "E109", {"start": v(-23.59, 20.96) * mm, "mid": v(-24.19, 21.41) * mm, "end": v(-24.94, 21.48) * mm});
            skFitSpline(sketch, "E110", {"points": [v(-24.94, 21.48) * mm, v(-24.61, 21.08) * mm, v(-24.25, 20.78) * mm, v(-23.83, 20.5) * mm], "startDerivative": vector(0.91, -1.25) * mm, "endDerivative": vector(1.28, -0.83) * mm});
            skLineSegment(sketch, "E111", {"start": v(-23.83, 20.5) * mm, "end": v(-23.59, 20.96) * mm});
            skFitSpline(sketch, "E112", {"points": [v(-6.3, 8.23) * mm, v(-6.51, 8.71) * mm, v(-6.85, 8.85) * mm, v(-7.11, 8.52) * mm, v(-7.11, 8.01) * mm, v(-6.85, 7.41) * mm, v(-6.44, 6.93) * mm, v(-6.32, 6.07) * mm, v(-6.37, 5.23) * mm, v(-6.3, 3.9) * mm, v(-6.03, 3.21) * mm], "startDerivative": vector(-1.78, 5.97) * mm, "endDerivative": vector(2.89, -5.79) * mm});
            skFitSpline(sketch, "E113", {"points": [v(-6.3, 8.23) * mm, v(-5.97, 7.8) * mm, v(-5.55, 7.15) * mm, v(-5.42, 6.53) * mm, v(-5.51, 5.83) * mm, v(-5.73, 5.17) * mm, v(-5.9, 4.41) * mm, v(-6.03, 3.21) * mm], "startDerivative": vector(2.52, -3.38) * mm, "endDerivative": vector(-0.69, -7) * mm});
            skFitSpline(sketch, "E114", {"points": [v(-3.64, 3.42) * mm, v(-3.11, 4.41) * mm, v(-2.3, 5.27) * mm, v(-1.73, 5.6) * mm, v(-1.36, 5.82) * mm, v(-0.78, 6.07) * mm, v(-0.53, 5.75) * mm, v(-0.66, 5.4) * mm, v(-1.2, 5) * mm, v(-1.66, 4.97) * mm, v(-2.26, 4.62) * mm, v(-2.86, 4.12) * mm, v(-3.64, 3.42) * mm]});
            skFitSpline(sketch, "E115", {"points": [v(0.52, 5.47) * mm, v(0, 5.2) * mm], "startDerivative": vector(-0.52, -0.28) * mm, "endDerivative": vector(-0.52, -0.28) * mm});
            skFitSpline(sketch, "E116", {"points": [v(0, 5.2) * mm, v(0.5, 4.79) * mm, v(0.9, 4.6) * mm, v(1.34, 4.29) * mm], "startDerivative": vector(1.4, -1.29) * mm, "endDerivative": vector(1.3, -1.08) * mm});
            skFitSpline(sketch, "E117", {"points": [v(1.34, 4.29) * mm, v(1.6, 4.57) * mm, v(1.6, 4.94) * mm, v(1.08, 5.2) * mm, v(0.52, 5.47) * mm], "startDerivative": vector(1.31, 1.12) * mm, "endDerivative": vector(-1.83, 1.05) * mm});
            skFitSpline(sketch, "E118", {"points": [v(2.96, 2.06) * mm, v(2.43, 2.83) * mm, v(2.59, 3.7) * mm, v(2.9, 4.29) * mm, v(3.02, 4.84) * mm, v(3.02, 5.2) * mm, v(2.9, 5.8) * mm, v(3.02, 6.57) * mm, v(3.79, 7.53) * mm, v(4.22, 8.33) * mm, v(4.96, 10) * mm], "startDerivative": vector(-6.55, 6.85) * mm, "endDerivative": vector(5.56, 12.42) * mm});
            skFitSpline(sketch, "E119", {"points": [v(4.96, 10) * mm, v(4.69, 8.55) * mm, v(4.5, 7.8) * mm, v(4.62, 6.88) * mm, v(4.22, 6.04) * mm, v(3.7, 5.2) * mm, v(3.26, 4.29) * mm, v(2.9, 3.42) * mm, v(2.96, 2.06) * mm], "startDerivative": vector(-1.6, -10.7) * mm, "endDerivative": vector(1.44, -10.17) * mm});
            skFitSpline(sketch, "E120", {"points": [v(11.23, 13.78) * mm, v(12.1, 14.54) * mm, v(13.59, 15.16) * mm, v(14.46, 15.64) * mm, v(16.1, 16.44) * mm, v(17.62, 16.92) * mm, v(19.01, 16.98) * mm], "startDerivative": vector(4.9, 5.4) * mm, "endDerivative": vector(8.43, -0.21) * mm});
            skFitSpline(sketch, "E121", {"points": [v(11.23, 13.78) * mm, v(12.07, 13.78) * mm, v(13.38, 13.78) * mm, v(14.33, 14.2) * mm, v(15.13, 14.8) * mm, v(16.21, 15.77) * mm, v(17.62, 16.6) * mm, v(19.01, 16.98) * mm], "startDerivative": vector(6.59, 0.2) * mm, "endDerivative": vector(8.98, 1.97) * mm});
            skFitSpline(sketch, "E122", {"points": [v(6.06, 9.6) * mm, v(7.64, 9.99) * mm, v(9.06, 10.41) * mm, v(10.57, 10.75) * mm, v(13, 10.88) * mm, v(15.13, 10.41) * mm, v(16.82, 10.7) * mm, v(19.37, 11.18) * mm, v(21.93, 10.58) * mm], "startDerivative": vector(14.16, 3.2) * mm, "endDerivative": vector(17.53, -6.09) * mm});
            skFitSpline(sketch, "E123", {"points": [v(6.06, 9.6) * mm, v(7.5, 9) * mm, v(9.72, 9.22) * mm, v(11.63, 9.6) * mm, v(13.59, 10.07) * mm], "startDerivative": vector(5.93, -3.45) * mm, "endDerivative": vector(7.75, 1.93) * mm});
            skFitSpline(sketch, "E124", {"points": [v(13.67, 10.07) * mm, v(15.13, 9.6) * mm, v(16.6, 9.6) * mm, v(18.55, 10.07) * mm, v(20.31, 10.5) * mm, v(21.93, 10.58) * mm], "startDerivative": vector(7.61, -2.98) * mm, "endDerivative": vector(8.22, 0.05) * mm});
            skFitSpline(sketch, "E125", {"points": [v(9.57, 12.14) * mm, v(10.35, 12.63) * mm, v(11.2, 12.9) * mm, v(12.27, 12.98) * mm, v(13.58, 12.8) * mm, v(13.58, 12.78) * mm], "startDerivative": vector(3.38, 2.38) * mm, "endDerivative": vector(-0.34, -0.65) * mm});
            skFitSpline(sketch, "E126", {"points": [v(13.58, 12.78) * mm, v(14.34, 13.12) * mm, v(16.09, 13.15) * mm, v(17.81, 13.17) * mm, v(19.83, 13.12) * mm, v(20.67, 12.98) * mm], "startDerivative": vector(4.25, 2.69) * mm, "endDerivative": vector(4.65, -1.07) * mm});
            skFitSpline(sketch, "E127", {"points": [v(20.67, 12.98) * mm, v(18.9, 12.93) * mm, v(17.34, 12.66) * mm, v(16.5, 12.48) * mm, v(15.28, 12.44) * mm, v(14.02, 12.41) * mm, v(13.2, 12.07) * mm, v(11.8, 11.9) * mm, v(10.38, 11.94) * mm, v(9.57, 12.14) * mm], "startDerivative": vector(-13.23, 0.13) * mm, "endDerivative": vector(-8.21, 2.5) * mm});
            skFitSpline(sketch, "E128", {"points": [v(-0.6, 3.92) * mm, v(-0.36, 3.46) * mm, v(-0.36, 2.78) * mm, v(-0.4, 2.1) * mm, v(-0.36, 1.07) * mm, v(-0.6, 0) * mm, v(-1.21, -0.83) * mm], "startDerivative": vector(2.32, -3.21) * mm, "endDerivative": vector(-3.67, -4.18) * mm});
            skFitSpline(sketch, "E129", {"points": [v(-1.21, -0.83) * mm, v(-1.21, 0) * mm, v(-1.01, 0.77) * mm, v(-0.92, 1.59) * mm, v(-0.9, 2.44) * mm, v(-0.74, 3.12) * mm, v(-0.6, 3.92) * mm], "startDerivative": vector(-0.36, 4.95) * mm, "endDerivative": vector(0.68, 4.94) * mm});
            skFitSpline(sketch, "E130", {"points": [v(22.04, 12.72) * mm, v(21.46, 12.46) * mm, v(21, 11.74) * mm], "startDerivative": vector(-1.34, -0.36) * mm, "endDerivative": vector(-0.77, -1.55) * mm});
            skFitSpline(sketch, "E131", {"points": [v(21, 11.74) * mm, v(22.04, 12.21) * mm, v(23.05, 12.25) * mm, v(24.27, 12.21) * mm], "startDerivative": vector(3.1, 1.73) * mm, "endDerivative": vector(3.6, -0.08) * mm});
            skFitSpline(sketch, "E132", {"points": [v(24.27, 12.21) * mm, v(24.27, 12.72) * mm, v(23.63, 12.97) * mm, v(22.65, 13.15) * mm, v(21.68, 13.08) * mm], "startDerivative": vector(0.63, 2.85) * mm, "endDerivative": vector(-3.48, -0.5) * mm});
            skFitSpline(sketch, "E133", {"points": [v(21.68, 13.08) * mm, v(22.04, 12.9) * mm, v(22.04, 12.72) * mm], "startDerivative": vector(0.8, -0.23) * mm, "endDerivative": vector(-0.12, -0.5) * mm});
            skFitSpline(sketch, "E134", {"points": [v(-8.13, 10.12) * mm, v(-9.16, 10.04) * mm, v(-10.95, 10.04) * mm, v(-12.58, 10.24) * mm, v(-13.42, 10.6) * mm], "startDerivative": vector(-4.33, -0.42) * mm, "endDerivative": vector(-3.65, 1.92) * mm});
            skFitSpline(sketch, "E135", {"points": [v(-13.42, 10.6) * mm, v(-14.85, 10.56) * mm, v(-16.12, 10.6) * mm, v(-18.47, 10.88) * mm, v(-20.42, 11.28) * mm], "startDerivative": vector(-6.55, -0.23) * mm, "endDerivative": vector(-6.92, 1.57) * mm});
            skFitSpline(sketch, "E136", {"points": [v(-20.42, 11.28) * mm, v(-19.94, 10.8) * mm, v(-18.47, 10.16) * mm, v(-16.36, 9.84) * mm, v(-14.7, 9.72) * mm, v(-13.38, 9.84) * mm], "startDerivative": vector(2.84, -3.5) * mm, "endDerivative": vector(6.7, 0.9) * mm});
            skFitSpline(sketch, "E137", {"points": [v(-13.38, 9.84) * mm, v(-11.75, 9.13) * mm, v(-10.2, 8.97) * mm, v(-8.76, 9.13) * mm, v(-8.13, 10.12) * mm], "startDerivative": vector(5.97, -3.15) * mm, "endDerivative": vector(2.12, 5.38) * mm});
            skFitSpline(sketch, "E138", {"points": [v(-13.22, 11.91) * mm, v(-13.3, 12.3) * mm, v(-13.79, 12.52) * mm, v(-14.64, 12.72) * mm, v(-15.66, 12.86) * mm, v(-17.29, 12.86) * mm, v(-19.06, 12.76) * mm, v(-19.74, 12.69) * mm, v(-20.62, 12.86) * mm, v(-21.33, 12.93) * mm], "startDerivative": vector(-0.2, 5.8) * mm, "endDerivative": vector(-6.87, 0.31) * mm});
            skFitSpline(sketch, "E139", {"points": [v(-21.33, 12.93) * mm, v(-20.1, 12.42) * mm, v(-18.47, 12.35) * mm, v(-16.68, 12.32) * mm, v(-15.18, 11.9) * mm, v(-14, 11.67) * mm, v(-13.22, 11.91) * mm], "startDerivative": vector(7.12, -3.75) * mm, "endDerivative": vector(5.69, 2.65) * mm});
            skFitSpline(sketch, "E140", {"points": [v(-26.67, 14) * mm, v(-26.11, 13.36) * mm, v(-25.14, 13.27) * mm, v(-24.3, 13.27) * mm, v(-23.42, 12.76) * mm, v(-22.98, 13) * mm, v(-23.28, 13.46) * mm, v(-23.9, 13.87) * mm, v(-24.34, 13.94) * mm, v(-24.92, 13.92) * mm, v(-25.48, 13.87) * mm, v(-26.19, 14.07) * mm, v(-26.67, 14) * mm]});
            skFitSpline(sketch, "E141", {"points": [v(-26.72, 12.06) * mm, v(-25.99, 11.76) * mm, v(-24.89, 11.46) * mm, v(-23.63, 11.42) * mm, v(-22.7, 11.63) * mm, v(-22.1, 11.53) * mm, v(-22.05, 11.12) * mm, v(-22.43, 10.82) * mm, v(-23.27, 10.71) * mm, v(-24.5, 10.77) * mm, v(-25.54, 11.08) * mm, v(-26.42, 11.53) * mm, v(-26.72, 12.06) * mm]});
            skFitSpline(sketch, "E142", {"points": [v(22.63, 11.28) * mm, v(23.23, 11.36) * mm, v(24.12, 11.36) * mm, v(25.01, 11.17) * mm, v(25.43, 10.8) * mm], "startDerivative": vector(2.52, 0.4) * mm, "endDerivative": vector(1.63, -1.88) * mm});
            skFitSpline(sketch, "E143", {"points": [v(25.43, 10.8) * mm, v(24.46, 10.7) * mm, v(23.73, 10.76) * mm, v(23, 10.97) * mm, v(22.63, 11.28) * mm], "startDerivative": vector(-3.48, -0.5) * mm, "endDerivative": vector(-1.54, 1.68) * mm});
            skLineSegment(sketch, "E144", {"start": v(25.27, 12.17) * mm, "end": v(25.97, 12.08) * mm});
            skArc(sketch, "E145", {"start": v(25.27, 12.17) * mm, "mid": v(25.6, 11.95) * mm, "end": v(25.97, 12.08) * mm});
            skFitSpline(sketch, "E146", {"points": [v(23.78, 13.34) * mm, v(24.52, 13.04) * mm, v(25.58, 12.72) * mm, v(26.3, 12.78) * mm, v(26.08, 13.16) * mm, v(25.32, 13.36) * mm, v(24.44, 13.52) * mm, v(23.78, 13.34) * mm]});
            skFitSpline(sketch, "E147", {"points": [v(20.92, 18.19) * mm, v(22.06, 18.5) * mm, v(22.93, 18.89) * mm, v(23.34, 19.47) * mm, v(23.73, 19.8) * mm, v(24.02, 19.78) * mm], "startDerivative": vector(4.42, 1.16) * mm, "endDerivative": vector(2.2, -0.56) * mm});
            skFitSpline(sketch, "E148", {"points": [v(24.02, 19.78) * mm, v(24.08, 20) * mm, v(24.4, 20.1) * mm, v(24.86, 19.8) * mm, v(24.58, 19.57) * mm], "startDerivative": vector(0.1, 1.17) * mm, "endDerivative": vector(-1.7, -0.84) * mm});
            skFitSpline(sketch, "E149", {"points": [v(24.58, 19.57) * mm, v(24.18, 19.43) * mm, v(24, 19.12) * mm, v(24, 18.83) * mm, v(23.42, 18.62) * mm, v(22.84, 18.38) * mm, v(22.1, 18.17) * mm, v(20.92, 18.19) * mm], "startDerivative": vector(-3.62, -0.67) * mm, "endDerivative": vector(-6.12, 0.47) * mm});
            skFitSpline(sketch, "E150", {"points": [v(20.92, 19.4) * mm, v(20.5, 19) * mm, v(20.12, 18.62) * mm, v(20.16, 18.4) * mm, v(20.76, 18.54) * mm, v(21.4, 18.83) * mm, v(21.65, 19.24) * mm, v(22.02, 19.65) * mm, v(22.68, 19.8) * mm, v(23.15, 20.1) * mm], "startDerivative": vector(-3.34, -3.43) * mm, "endDerivative": vector(3.73, 3.09) * mm});
            skFitSpline(sketch, "E151", {"points": [v(23.15, 20.1) * mm, v(22.04, 20.1) * mm, v(20.74, 19.88) * mm, v(20.02, 19.57) * mm], "startDerivative": vector(-3.1, 0.11) * mm, "endDerivative": vector(-2.26, -1.17) * mm});
            skFitSpline(sketch, "E152", {"points": [v(20.02, 19.57) * mm, v(20.92, 19.4) * mm], "startDerivative": vector(0.9, -0.17) * mm, "endDerivative": vector(0.9, -0.17) * mm});
            skFitSpline(sketch, "E153", {"points": [v(22.65, 20.58) * mm, v(22.5, 20.8) * mm, v(22.65, 21.03) * mm, v(22.93, 21.14) * mm, v(23.29, 21.27) * mm, v(23.62, 21.37) * mm, v(24.01, 21.37) * mm, v(24.31, 21.27) * mm, v(24.17, 20.98) * mm, v(23.77, 20.89) * mm, v(23.26, 20.9) * mm, v(22.84, 20.84) * mm, v(22.65, 20.58) * mm]});
            skFitSpline(sketch, "E154", {"points": [v(-4.6, 4.86) * mm, v(-4.41, 3.94) * mm, v(-4.55, 2) * mm, v(-4.92, 1) * mm, v(-4.82, 0) * mm, v(-4.73, -1.44) * mm, v(-5.47, -3.55) * mm, v(-5.74, -5.58) * mm, v(-5.65, -7.32) * mm, v(-5.38, -9.72) * mm, v(-5.38, -11.78) * mm, v(-5.97, -13.67) * mm], "startDerivative": vector(3.27, -11.72) * mm, "endDerivative": vector(-7.46, -18.9) * mm});
            skFitSpline(sketch, "E155", {"points": [v(-5.97, -13.67) * mm, v(-5.84, -11.42) * mm, v(-6.34, -8.84) * mm, v(-6.7, -6.31) * mm, v(-6.66, -3.74) * mm, v(-6.11, -1.8) * mm, v(-5.84, -0.52) * mm, v(-5.97, 0.9) * mm, v(-5.65, 2.24) * mm, v(-5, 3.16) * mm], "startDerivative": vector(2.45, 18.16) * mm, "endDerivative": vector(8.14, 9.91) * mm});
            skFitSpline(sketch, "E156", {"points": [v(-5, 3.16) * mm, v(-4.77, 3.74) * mm, v(-4.76, 4.22) * mm, v(-4.8, 4.6) * mm, v(-4.83, 4.84) * mm], "startDerivative": vector(1, 1.94) * mm, "endDerivative": vector(-0.23, 1.18) * mm});
            skLineSegment(sketch, "E157", {"start": v(-4.83, 4.84) * mm, "end": v(-4.6, 4.86) * mm});
            skFitSpline(sketch, "E158", {"points": [v(-4.78, -8.44) * mm, v(-4.55, -7.83) * mm, v(-4.12, -7.56) * mm, v(-3.63, -6.9) * mm, v(-3.01, -6.06) * mm, v(-2.13, -4.8) * mm], "startDerivative": vector(0.9, 4.15) * mm, "endDerivative": vector(3.44, 5.05) * mm});
            skFitSpline(sketch, "E159", {"points": [v(-2.13, -4.8) * mm, v(-1.82, -5.14) * mm, v(-1.9, -5.87) * mm, v(-1.13, -5.95) * mm, v(-0.67, -5.37) * mm, v(-0.4, -5.03) * mm], "startDerivative": vector(2.54, -1.54) * mm, "endDerivative": vector(1.63, 1.79) * mm});
            skFitSpline(sketch, "E160", {"points": [v(-0.4, -5.03) * mm, v(-0.4, -5.59) * mm, v(-0.57, -6.21) * mm, v(-1.06, -6.47) * mm], "startDerivative": vector(0.05, -1.63) * mm, "endDerivative": vector(-1.74, -0.54) * mm});
            skFitSpline(sketch, "E161", {"points": [v(-1.06, -6.47) * mm, v(-1.18, -6.6) * mm, v(-1.04, -6.88) * mm, v(-1.06, -7.22) * mm, v(-1.53, -7.26) * mm, v(-1.99, -7.13) * mm], "startDerivative": vector(-1.23, -0.86) * mm, "endDerivative": vector(-1.8, 0.67) * mm});
            skFitSpline(sketch, "E162", {"points": [v(-1.99, -7.13) * mm, v(-2.11, -6.78) * mm, v(-2.3, -6.29) * mm], "startDerivative": vector(-0.24, 0.74) * mm, "endDerivative": vector(-0.4, 0.93) * mm});
            skFitSpline(sketch, "E163", {"points": [v(-2.3, -6.29) * mm, v(-2.83, -6.87) * mm, v(-3.32, -7.4) * mm, v(-3.93, -7.86) * mm, v(-4.3, -8) * mm, v(-4.58, -8.24) * mm, v(-4.78, -8.44) * mm], "startDerivative": vector(-2.64, -2.91) * mm, "endDerivative": vector(-1.56, -1.56) * mm});
            skFitSpline(sketch, "E164", {"points": [v(0.66, -6.85) * mm, v(0.52, -6.47) * mm, v(0.52, -5.9) * mm, v(0.73, -5.17) * mm, v(0.73, -4.75) * mm, v(0.54, -4.42) * mm, v(0.23, -4.14) * mm, v(0.23, -3.93) * mm], "startDerivative": vector(-1.17, 2.63) * mm, "endDerivative": vector(0.54, 2.17) * mm});
            skFitSpline(sketch, "E165", {"points": [v(0.23, -3.93) * mm, v(0.6, -3.95) * mm, v(0.9, -4.12) * mm, v(0.92, -4.75) * mm, v(1, -5.4) * mm, v(1, -6.05) * mm, v(0.92, -6.54) * mm, v(0.66, -6.85) * mm], "startDerivative": vector(2.93, 0.05) * mm, "endDerivative": vector(-2.35, -2.21) * mm});
            skFitSpline(sketch, "E166", {"points": [v(3.11, 1.08) * mm, v(2.63, 0) * mm, v(2.71, -2.03) * mm, v(2.71, -4.22) * mm, v(2.75, -6.54) * mm, v(2.35, -9.4) * mm, v(1.44, -12.4) * mm, v(1.29, -13.45) * mm, v(1.65, -13.54) * mm, v(2.1, -12.47) * mm, v(2.61, -10.67) * mm, v(2.99, -8.79) * mm, v(3.23, -5.63) * mm, v(3.2, -3.2) * mm, v(3.03, -1.52) * mm, v(3.15, 0) * mm, v(3.11, 1.08) * mm]});
            skFitSpline(sketch, "E167", {"points": [v(4.04, -0.31) * mm, v(3.88, -1.33) * mm, v(4.33, -2.92) * mm, v(5.02, -5.27) * mm, v(5.7, -7.47) * mm, v(5.95, -10.36) * mm], "startDerivative": vector(-1.96, -6.83) * mm, "endDerivative": vector(0.38, -12.58) * mm});
            skFitSpline(sketch, "E168", {"points": [v(5.95, -10.36) * mm, v(6.25, -8.35) * mm, v(6.14, -6.48) * mm, v(5.37, -4.6) * mm, v(4.7, -2.98) * mm, v(4.15, -1.33) * mm, v(4.04, -0.31) * mm], "startDerivative": vector(2.03, 11.17) * mm, "endDerivative": vector(-0.27, 7.44) * mm});
            skFitSpline(sketch, "E169", {"points": [v(-9.35, -11.03) * mm, v(-8.84, -10.07) * mm, v(-8.34, -9.66) * mm, v(-7.86, -9.19) * mm, v(-7.32, -8.24) * mm], "startDerivative": vector(1.65, 3.85) * mm, "endDerivative": vector(1.87, 3.69) * mm});
            skFitSpline(sketch, "E170", {"points": [v(-7.32, -8.17) * mm, v(-7.1, -9.06) * mm, v(-7.39, -9.98) * mm, v(-8.02, -10.36) * mm, v(-8.78, -10.87) * mm, v(-9.35, -11.03) * mm], "startDerivative": vector(1.53, -4) * mm, "endDerivative": vector(-3.3, -0.5) * mm});
            skFitSpline(sketch, "E171", {"points": [v(-16.15, -21.64) * mm, v(-15.51, -20.01) * mm, v(-15.46, -18.3) * mm, v(-14.63, -16.08) * mm, v(-13.3, -15.2) * mm, v(-12.9, -15) * mm], "startDerivative": vector(3.8, 7.49) * mm, "endDerivative": vector(3, 1.56) * mm});
            skFitSpline(sketch, "E172", {"points": [v(-12.9, -15) * mm, v(-12.9, -15.53) * mm, v(-13.5, -16.44) * mm, v(-14.08, -17.65) * mm, v(-14.57, -18.73) * mm, v(-15.14, -19.94) * mm, v(-16.15, -21.64) * mm], "startDerivative": vector(0.87, -4.7) * mm, "endDerivative": vector(-5.2, -8.2) * mm});
            skFitSpline(sketch, "E173", {"points": [v(-16.28, -22.58) * mm, v(-16.6, -23.19) * mm, v(-17.23, -23.75) * mm, v(-17.77, -24.27) * mm, v(-17.87, -24.62) * mm, v(-17.38, -24.66) * mm, v(-17.16, -24.66) * mm], "startDerivative": vector(-1.35, -3.31) * mm, "endDerivative": vector(1.58, -0.1) * mm});
            skFitSpline(sketch, "E174", {"points": [v(-17.16, -24.66) * mm, v(-16.93, -25) * mm, v(-16.56, -25.2) * mm, v(-16, -24.9) * mm, v(-15.57, -24.55) * mm], "startDerivative": vector(0.9, -1.53) * mm, "endDerivative": vector(1.5, 1.29) * mm});
            skFitSpline(sketch, "E175", {"points": [v(-15.57, -24.55) * mm, v(-15.4, -24.94) * mm, v(-15.57, -25.45) * mm, v(-16.2, -25.8) * mm, v(-17.15, -25.54) * mm, v(-17.59, -25.24) * mm, v(-18.1, -25.17) * mm, v(-18.58, -25.19) * mm], "startDerivative": vector(2, -3.01) * mm, "endDerivative": vector(-3.6, -0.2) * mm});
            skFitSpline(sketch, "E176", {"points": [v(-18.58, -25.19) * mm, v(-18.83, -24.92) * mm, v(-18.6, -24.55) * mm, v(-18.09, -24.05) * mm, v(-17.34, -23.54) * mm, v(-16.72, -22.94) * mm, v(-16.28, -22.58) * mm], "startDerivative": vector(-2.8, 1.96) * mm, "endDerivative": vector(2.75, 2) * mm});
            skFitSpline(sketch, "E177", {"points": [v(-5.08, -25.72) * mm, v(-5.24, -23.73) * mm, v(-5.92, -21) * mm, v(-6.08, -18.5) * mm, v(-5.87, -16.5) * mm, v(-5.45, -14.57) * mm, v(-4.56, -14.57) * mm, v(-4.42, -15.33) * mm, v(-5.04, -16.96) * mm, v(-5.7, -19.35) * mm, v(-5.67, -20.73) * mm, v(-5.15, -22.8) * mm, v(-4.8, -25.17) * mm, v(-5.08, -25.72) * mm]});
            skFitSpline(sketch, "E178", {"points": [v(-14.92, -23.4) * mm, v(-14.74, -21.46) * mm, v(-14.26, -20.56) * mm, v(-12.8, -18.58) * mm, v(-11.97, -17.03) * mm, v(-11.2, -15.43) * mm, v(-10.24, -14.05) * mm, v(-9.34, -13.04) * mm, v(-8.23, -12.07) * mm, v(-7.33, -11.38) * mm, v(-6.91, -10.79) * mm, v(-6.32, -10.27) * mm], "startDerivative": vector(0.67, 20.55) * mm, "endDerivative": vector(9.61, 7.24) * mm});
            skFitSpline(sketch, "E179", {"points": [v(-6.32, -10.27) * mm, v(-6.84, -11.07) * mm, v(-7.22, -12.04) * mm, v(-8.16, -13.11) * mm, v(-9.27, -14.01) * mm], "startDerivative": vector(-2.62, -3.43) * mm, "endDerivative": vector(-4.08, -3.16) * mm});
            skFitSpline(sketch, "E180", {"points": [v(-9.27, -14.01) * mm, v(-10.07, -15.57) * mm, v(-11.07, -17.48) * mm, v(-11.94, -18.62) * mm, v(-12.84, -19.55) * mm, v(-14.12, -21.53) * mm, v(-14.92, -23.4) * mm], "startDerivative": vector(-4.72, -9.11) * mm, "endDerivative": vector(-3.92, -10.36) * mm});
            skFitSpline(sketch, "E181", {"points": [v(-4.13, -26.66) * mm, v(-4.55, -27.82) * mm, v(-4.7, -28.83) * mm, v(-4.71, -29.59) * mm], "startDerivative": vector(-1.29, -3.13) * mm, "endDerivative": vector(0.02, -2.52) * mm});
            skFitSpline(sketch, "E182", {"points": [v(-4.71, -29.59) * mm, v(-4.1, -29.57) * mm, v(-3.13, -29.67) * mm, v(-2.2, -29.67) * mm, v(-1.54, -29.51) * mm], "startDerivative": vector(2.65, 0.17) * mm, "endDerivative": vector(2.72, 0.84) * mm});
            skFitSpline(sketch, "E183", {"points": [v(-1.54, -29.51) * mm, v(-1.53, -28.95) * mm, v(-1.74, -28.14) * mm, v(-1.93, -27.78) * mm, v(-2.05, -27.4) * mm], "startDerivative": vector(0.2, 2.02) * mm, "endDerivative": vector(-0.5, 1.87) * mm});
            skFitSpline(sketch, "E184", {"points": [v(-2.05, -27.4) * mm, v(-2.05, -28.1) * mm, v(-2.06, -28.77) * mm, v(-2.35, -29.19) * mm, v(-2.67, -29.36) * mm, v(-3.1, -29.26) * mm, v(-3.32, -29.08) * mm, v(-3.62, -28.85) * mm], "startDerivative": vector(-0.11, -3.95) * mm, "endDerivative": vector(-2.52, 1.75) * mm});
            skFitSpline(sketch, "E185", {"points": [v(-3.62, -28.85) * mm, v(-3.97, -28.95) * mm, v(-4.35, -29.01) * mm, v(-4.45, -28.58) * mm, v(-4.33, -27.7) * mm, v(-4.2, -27.27) * mm, v(-4.13, -26.66) * mm], "startDerivative": vector(-2.32, -0.6) * mm, "endDerivative": vector(0.15, 3.6) * mm});
            skFitSpline(sketch, "E186", {"points": [v(-3.42, -11.6) * mm, v(-3.28, -10.67) * mm, v(-3.15, -9.92) * mm, v(-2.83, -9.4) * mm, v(-2.7, -10.08) * mm, v(-2.85, -10.83) * mm, v(-3.04, -11.4) * mm, v(-3.42, -11.6) * mm]});
            skFitSpline(sketch, "E187", {"points": [v(-1.54, -8.3) * mm, v(-1.75, -9.54) * mm, v(-2.18, -10.8) * mm, v(-2.34, -11.55) * mm, v(-2.23, -12.01) * mm, v(-2.26, -12.7) * mm, v(-2.64, -13.4) * mm, v(-3.07, -14.21) * mm, v(-2.99, -15.18) * mm, v(-3.15, -16.04) * mm, v(-3.76, -17.83) * mm, v(-3.84, -18.7) * mm], "startDerivative": vector(-1.47, -11.73) * mm, "endDerivative": vector(0.06, -8.72) * mm});
            skFitSpline(sketch, "E188", {"points": [v(-3.84, -18.7) * mm, v(-3.04, -17.91) * mm, v(-2.72, -16.92) * mm, v(-2.53, -16.44) * mm, v(-2.66, -15.82) * mm, v(-2.66, -15.04) * mm, v(-2.45, -13.97) * mm, v(-2.13, -13.22) * mm, v(-1.97, -12.6) * mm, v(-2, -11.72) * mm, v(-2, -11.15) * mm, v(-1.8, -10.4) * mm, v(-1.51, -9.54) * mm, v(-1.54, -8.3) * mm], "startDerivative": vector(10.54, 7.62) * mm, "endDerivative": vector(-1.46, 13.9) * mm});
            skFitSpline(sketch, "E189", {"points": [v(-0.81, -9.6) * mm, v(-0.5, -10.17) * mm, v(-0.47, -11.09) * mm, v(-0.68, -12.38) * mm, v(-1.02, -13.53) * mm, v(-1.12, -14.48) * mm, v(-1.02, -15.33) * mm, v(-0.92, -16.51) * mm, v(-1.5, -18.08) * mm, v(-1.8, -19.7) * mm, v(-1.5, -22.25) * mm, v(-1.12, -24.05) * mm, v(-1.08, -25.84) * mm], "startDerivative": vector(6.27, -9.23) * mm, "endDerivative": vector(-0.56, -18.97) * mm});
            skFitSpline(sketch, "E190", {"points": [v(-1.08, -25.84) * mm, v(-1.26, -24.73) * mm, v(-1.5, -23.8) * mm, v(-1.84, -22.53) * mm, v(-2.16, -21.51) * mm, v(-2.3, -20.34) * mm, v(-2.12, -18.9) * mm, v(-1.8, -17.33) * mm, v(-1.85, -16.2) * mm, v(-1.85, -15.07) * mm, v(-1.5, -14.48) * mm], "startDerivative": vector(-1.52, 11.72) * mm, "endDerivative": vector(5.58, 6.7) * mm});
            skFitSpline(sketch, "E191", {"points": [v(-1.5, -14.48) * mm, v(-1.5, -13.83) * mm, v(-1.5, -12.6) * mm, v(-1.5, -11.38) * mm, v(-1.22, -10.22) * mm, v(-0.81, -9.6) * mm], "startDerivative": vector(-0.02, 3.68) * mm, "endDerivative": vector(2.52, 3.22) * mm});
            skFitSpline(sketch, "E192", {"points": [v(-2.66, -25.78) * mm, v(-3.27, -24.19) * mm, v(-3.43, -22.26) * mm, v(-3.43, -20.42) * mm, v(-3.43, -19.2) * mm], "startDerivative": vector(-2.85, 6.1) * mm, "endDerivative": vector(0, 5.43) * mm});
            skFitSpline(sketch, "E193", {"points": [v(-3.43, -19.2) * mm, v(-2.94, -19.72) * mm, v(-3.02, -21.16) * mm, v(-3.07, -22.47) * mm, v(-3.02, -24.19) * mm, v(-2.74, -25.18) * mm, v(-2.66, -25.78) * mm], "startDerivative": vector(4.57, -3.09) * mm, "endDerivative": vector(0.33, -4.7) * mm});
            skFitSpline(sketch, "E194", {"points": [v(-0.2, -29.45) * mm, v(-0.46, -29.16) * mm, v(-0.53, -28.57) * mm, v(-0.55, -27.56) * mm, v(-0.63, -26.96) * mm, v(-0.87, -26.56) * mm], "startDerivative": vector(-1.92, 1.56) * mm, "endDerivative": vector(-1.58, 2.18) * mm});
            skFitSpline(sketch, "E195", {"points": [v(-0.87, -26.56) * mm, v(-0.55, -26.8) * mm, v(-0.38, -27.47) * mm, v(-0.33, -28.48) * mm, v(-0.18, -29.08) * mm, v(0.36, -29.01) * mm, v(1.2, -28.83) * mm, v(1.9, -28.8) * mm, v(2.93, -29.17) * mm, v(3.97, -29.4) * mm, v(5.15, -29.38) * mm], "startDerivative": vector(4.94, -2.62) * mm, "endDerivative": vector(9.9, 0.73) * mm});
            skFitSpline(sketch, "E196", {"points": [v(5.15, -29.38) * mm, v(4.45, -29.83) * mm, v(3.78, -30) * mm, v(3.23, -29.77) * mm, v(2.47, -29.47) * mm, v(1.8, -29.19) * mm, v(1.08, -29.36) * mm, v(0.45, -29.49) * mm, v(-0.2, -29.45) * mm], "startDerivative": vector(-4.97, -3.67) * mm, "endDerivative": vector(-5.49, 0.57) * mm});
            skFitSpline(sketch, "E197", {"points": [v(-0.2, -25.52) * mm, v(-0.2, -26.29) * mm, v(-0.1, -27.08) * mm, v(0.17, -27.37) * mm, v(0.36, -27.34) * mm, v(0.45, -26.94) * mm, v(0.23, -26.56) * mm, v(0.02, -26.14) * mm, v(-0.2, -25.52) * mm]});
            skFitSpline(sketch, "E198", {"points": [v(2.04, -26.3) * mm, v(1.73, -26.52) * mm, v(1.73, -26.92) * mm, v(2, -27.32) * mm, v(2.44, -27.54) * mm, v(3, -27.54) * mm, v(3.55, -27.8) * mm], "startDerivative": vector(-2.59, -1.16) * mm, "endDerivative": vector(2.85, -1.82) * mm});
            skFitSpline(sketch, "E199", {"points": [v(3.55, -27.8) * mm, v(2.91, -27.3) * mm, v(2.4, -26.87) * mm, v(2.16, -26.55) * mm, v(2.04, -26.3) * mm], "startDerivative": vector(-2.05, 1.61) * mm, "endDerivative": vector(-0.62, 1.3) * mm});
            skFitSpline(sketch, "E200", {"points": [v(-0.23, -23.02) * mm, v(0, -21.85) * mm, v(0, -20.45) * mm, v(-0.48, -19.2) * mm, v(-0.62, -17.7) * mm, v(-0.26, -17.2) * mm], "startDerivative": vector(1.29, 5.62) * mm, "endDerivative": vector(3.06, 2.75) * mm});
            skFitSpline(sketch, "E201", {"points": [v(-0.26, -17.2) * mm, v(0.12, -18.41) * mm, v(0.3, -19.68) * mm, v(0.33, -21.1) * mm, v(0.21, -22.38) * mm, v(-0.23, -23.02) * mm], "startDerivative": vector(2.82, -5.46) * mm, "endDerivative": vector(-3.21, -3.49) * mm});
            skFitSpline(sketch, "E202", {"points": [v(1, -25.52) * mm, v(1.5, -23.26) * mm, v(1.22, -21.51) * mm, v(1.1, -18.72) * mm, v(1.38, -16.46) * mm, v(1.76, -14.96) * mm, v(2.18, -14.53) * mm, v(2.57, -15.27) * mm, v(1.8, -16.84) * mm, v(1.6, -18.07) * mm, v(1.53, -19.53) * mm, v(1.65, -20.69) * mm, v(1.8, -22) * mm, v(1.88, -23.1) * mm, v(1.65, -24.41) * mm, v(1, -25.52) * mm]});
            skFitSpline(sketch, "E203", {"points": [v(8.18, -20.45) * mm, v(8.14, -21.1) * mm, v(8.49, -22.07) * mm, v(8.99, -22.65) * mm, v(9.07, -22) * mm, v(8.91, -21.34) * mm, v(8.57, -21.03) * mm, v(8.18, -20.45) * mm]});
            skFitSpline(sketch, "E204", {"points": [v(6.99, -15.73) * mm, v(6.72, -16.19) * mm, v(6.99, -16.96) * mm, v(7.64, -17.57) * mm, v(8.45, -18.72) * mm, v(9.22, -20.1) * mm, v(10.07, -21.92) * mm, v(10.64, -23.5) * mm], "startDerivative": vector(-3.9, -4.34) * mm, "endDerivative": vector(3.13, -9.18) * mm});
            skFitSpline(sketch, "E205", {"points": [v(10.64, -23.5) * mm, v(9.99, -20.76) * mm, v(9.03, -18.5) * mm, v(8.22, -16.88) * mm, v(6.99, -15.73) * mm], "startDerivative": vector(-1.89, 9.82) * mm, "endDerivative": vector(-6.14, 4.82) * mm});
            skLineSegment(sketch, "E206.bottom", {"start": v(-1.46, 15.5) * mm, "end": v(-1.02, 15.5) * mm});
            skLineSegment(sketch, "E206.top", {"start": v(-1.46, 15.36) * mm, "end": v(-1.02, 15.36) * mm});
            skLineSegment(sketch, "E206.left", {"start": v(-1.46, 15.5) * mm, "end": v(-1.46, 15.36) * mm});
            skLineSegment(sketch, "E206.right", {"start": v(-1.02, 15.5) * mm, "end": v(-1.02, 15.36) * mm});
            skLineSegment(sketch, "E207", {"start": v(-1.25, 18.85) * mm, "end": v(-1.25, 16.96) * mm});
            skFitSpline(sketch, "E208", {"points": [v(-1.25, 16.96) * mm, v(-0.97, 16.8) * mm, v(-0.85, 16.68) * mm, v(-1.1, 16.65) * mm, v(-1.32, 16.74) * mm, v(-1.57, 16.78) * mm], "startDerivative": vector(1.2, -0.68) * mm, "endDerivative": vector(-1.34, 0.08) * mm});
            skLineSegment(sketch, "E209", {"start": v(-1.57, 16.78) * mm, "end": v(-1.57, 17.93) * mm});
            skFitSpline(sketch, "E210", {"points": [v(-1.57, 17.93) * mm, v(-2.04, 17.93) * mm, v(-2.46, 18.04) * mm, v(-2.7, 18.09) * mm, v(-2.7, 18.3) * mm], "startDerivative": vector(-1.61, -0.15) * mm, "endDerivative": vector(0.2, 1.32) * mm});
            skFitSpline(sketch, "E211", {"points": [v(-2.7, 18.3) * mm, v(-2.27, 18.31) * mm, v(-1.94, 18.36) * mm, v(-2, 18.54) * mm, v(-2.42, 18.58) * mm, v(-2.88, 18.57) * mm], "startDerivative": vector(1.9, 0.1) * mm, "endDerivative": vector(-2, 0) * mm});
            skFitSpline(sketch, "E212", {"points": [v(-2.88, 18.57) * mm, v(-2.88, 18.75) * mm], "startDerivative": vector(0, 0.18) * mm, "endDerivative": vector(0, 0.18) * mm});
            skFitSpline(sketch, "E213", {"points": [v(-2.88, 18.75) * mm, v(-2.5, 18.85) * mm, v(-2.09, 18.87) * mm, v(-1.57, 18.87) * mm, v(-1.25, 18.85) * mm], "startDerivative": vector(1.59, 0.5) * mm, "endDerivative": vector(1.36, -0.11) * mm});
            skFitSpline(sketch, "E214", {"points": [v(-0.5, 18.2) * mm, v(-0.48, 18.85) * mm], "startDerivative": vector(0.01, 0.65) * mm, "endDerivative": vector(0.01, 0.65) * mm});
            skFitSpline(sketch, "E215", {"points": [v(-0.48, 18.88) * mm, v(-0.1, 18.9) * mm, v(0.33, 18.84) * mm, v(0.55, 18.56) * mm, v(0.55, 18.37) * mm], "startDerivative": vector(1.38, 0.09) * mm, "endDerivative": vector(-0.16, -0.97) * mm});
            skFitSpline(sketch, "E216", {"points": [v(0.55, 18.37) * mm, v(0.34, 18.36) * mm, v(0.27, 18.49) * mm, v(0.08, 18.5) * mm, v(0, 18.32) * mm, v(0.3, 18.27) * mm, v(0.5, 18.1) * mm], "startDerivative": vector(-1.54, -0.4) * mm, "endDerivative": vector(0.87, -1.2) * mm});
            skFitSpline(sketch, "E217", {"points": [v(0.5, 18.1) * mm, v(0.27, 18.1) * mm, v(0.09, 18.18) * mm, v(-0.2, 18.2) * mm, v(-0.5, 18.2) * mm], "startDerivative": vector(-1.05, -0.12) * mm, "endDerivative": vector(-1.06, 0) * mm});
            skFitSpline(sketch, "E218", {"points": [v(7.45, -11.8) * mm, v(7.52, -13.53) * mm, v(8.1, -15.3) * mm, v(9.53, -17.93) * mm, v(10.47, -19.78) * mm, v(11.16, -21.45) * mm, v(12.74, -23.7) * mm, v(13.67, -24.08) * mm], "startDerivative": vector(-0.27, -13.2) * mm, "endDerivative": vector(8.83, -1.58) * mm});
            skFitSpline(sketch, "E219", {"points": [v(13.67, -24.08) * mm, v(12.34, -22.5) * mm, v(11.72, -20.76) * mm, v(10.95, -18.73) * mm, v(9.99, -17) * mm, v(8.88, -15.05) * mm, v(7.89, -13.26) * mm, v(7.45, -11.8) * mm], "startDerivative": vector(-10.4, 10.41) * mm, "endDerivative": vector(-2.67, 11.48) * mm});
            skLineSegment(sketch, "E220", {"start": v(-7.32, -8.24) * mm, "end": v(-7.32, -8.17) * mm});
            skLineSegment(sketch, "E221", {"start": v(13.59, 10.07) * mm, "end": v(13.67, 10.07) * mm});
            skLineSegment(sketch, "E222", {"start": v(-0.48, 18.85) * mm, "end": v(-0.48, 18.88) * mm});
            skLineSegment(sketch, "E223", {"start": v(1.92, 14.69) * mm, "end": v(1.92, 14.67) * mm});
            skSolve(sketch);
        }
        {
            var Q0;
            Q0 = qSketchRegion(id + "F18", true);
            extrude(context, id + "F19", {"entities" : qUnion([Q0]), "operationType" : NewBodyOperationType.REMOVE, "oppositeDirection" : true, "depth" : 25.4 * mm});
        }
    });
